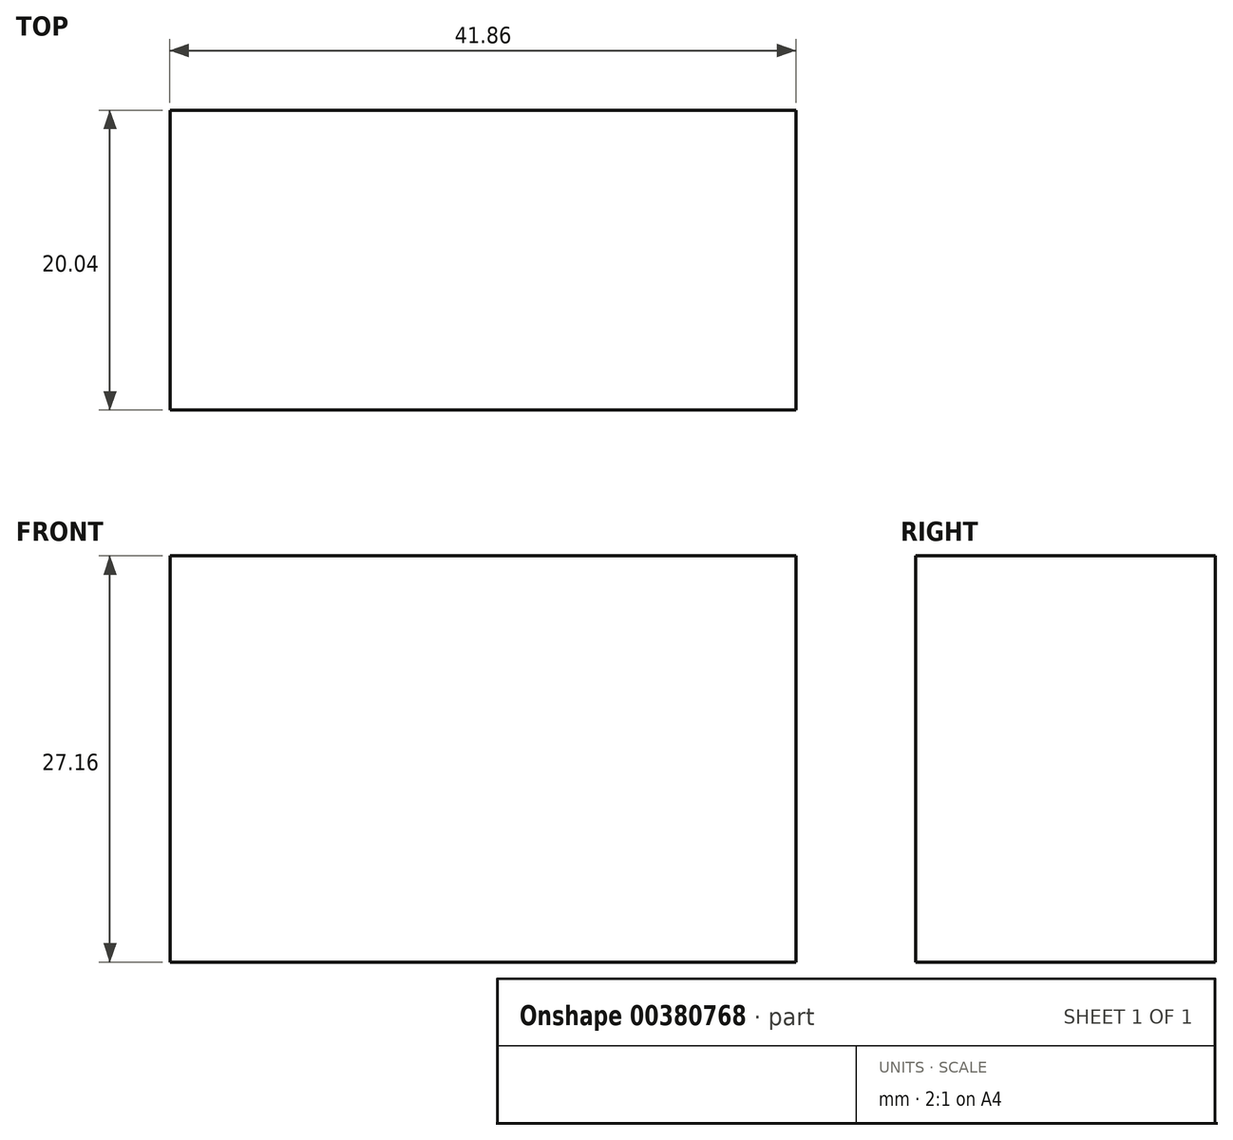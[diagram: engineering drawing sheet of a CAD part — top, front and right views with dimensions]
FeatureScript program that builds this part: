
annotation { "Feature Type Name" : "Feature", "Feature Type Description" : "" }
export const myFeature = defineFeature(function(context is Context, id is Id, definition is map)
    precondition{}
    {
        {
            var Q0;
            Q0=qCreatedBy(makeId("Front.planeOp"),FACE);
            var sketch = newSketch(context, id + "F0", { "sketchPlane" : qUnion([Q0])});
            skLineSegment(sketch, "E0.bottom", {"start": v(20.93, -13.59) * mm, "end": v(-20.93, -13.59) * mm});
            skLineSegment(sketch, "E0.top", {"start": v(20.93, 13.59) * mm, "end": v(-20.93, 13.59) * mm});
            skLineSegment(sketch, "E0.left", {"start": v(20.93, -13.58) * mm, "end": v(20.93, 13.59) * mm});
            skLineSegment(sketch, "E0.right", {"start": v(-20.93, -13.59) * mm, "end": v(-20.93, 13.58) * mm});
            skPoint(sketch, "E0.middle", {"position": v(0, 0) * mm});
            skSolve(sketch);
        }
        {
            var Q0;
            Q0=makeQuery(id+"F0.imprint","IMPRINT",FACE,{"disambiguationData":[TD([[makeQuery(id+"F0.imprint","IMPRINT",EDGE,{"derivedFrom":sQuery(id+"F0.wireOp",EDGE,"E0.bottom")}),-1.0]])]});
            extrude(context, id + "F1", {"entities" : qUnion([Q0]), "oppositeDirection" : true, "depth" : 20.04 * mm});
        }
        {
            var Q0;
            Q0=makeQuery(id+"F1.opExtrude","SWEPT_FACE",FACE,{"disambiguationData":[OSD([sQuery(id+"F0.wireOp",EDGE,"E0.left")])]});
            var sketch = newSketch(context, id + "F2", { "sketchPlane" : qUnion([Q0])});
            skLineSegment(sketch, "E1.bottom", {"start": v(7.2, -0.82) * mm, "end": v(13.14, -0.82) * mm});
            skLineSegment(sketch, "E1.top", {"start": v(7.2, -13.58) * mm, "end": v(13.14, -13.58) * mm});
            skLineSegment(sketch, "E1.left", {"start": v(7.2, -0.82) * mm, "end": v(7.2, -13.58) * mm});
            skLineSegment(sketch, "E1.right", {"start": v(13.14, -0.82) * mm, "end": v(13.14, -13.58) * mm});
            skSolve(sketch);
        }
        {
            var Q0;
            Q0=makeQuery(id+"F2.imprint","IMPRINT",FACE,{"disambiguationData":[TD([[makeQuery(id+"F2.imprint","IMPRINT",EDGE,{"derivedFrom":sQuery(id+"F2.wireOp",EDGE,"E1.bottom")}),-1.0]])]});
            extrude(context, id + "F3", {"entities" : qUnion([Q0]), "operationType" : NewBodyOperationType.ADD, "oppositeDirection" : true, "depth" : 11.92 * mm});
        }
    });
